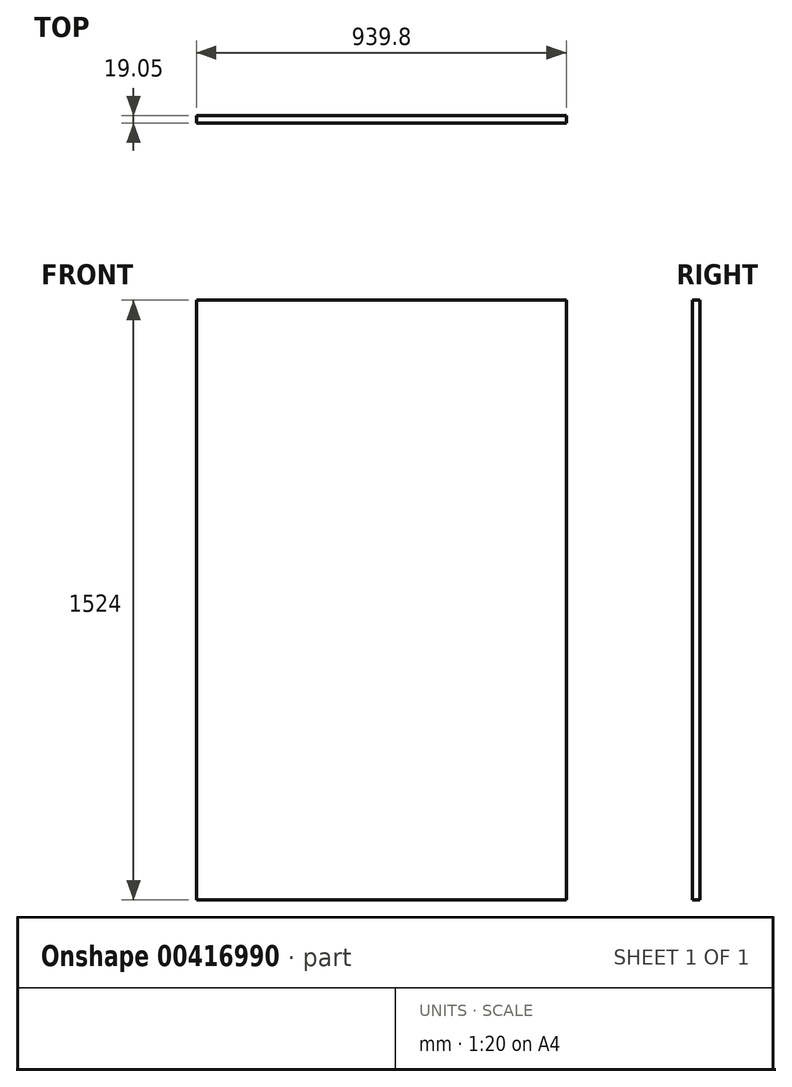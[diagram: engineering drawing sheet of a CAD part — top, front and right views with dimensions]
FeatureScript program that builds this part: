
annotation { "Feature Type Name" : "Feature", "Feature Type Description" : "" }
export const myFeature = defineFeature(function(context is Context, id is Id, definition is map)
    precondition{}
    {
        {
            var Q0;
            Q0=qCreatedBy(makeId("Front.planeOp"),FACE);
            var sketch = newSketch(context, id + "F0", { "sketchPlane" : qUnion([Q0])});
            skLineSegment(sketch, "E0.bottom", {"start": v(748.13, 187.42) * mm, "end": v(-191.67, 187.42) * mm});
            skLineSegment(sketch, "E0.top", {"start": v(748.13, -1336.58) * mm, "end": v(-191.67, -1336.58) * mm});
            skLineSegment(sketch, "E0.left", {"start": v(748.13, 187.42) * mm, "end": v(748.13, -1336.58) * mm});
            skLineSegment(sketch, "E0.right", {"start": v(-191.67, 187.42) * mm, "end": v(-191.67, -1336.58) * mm});
            skPoint(sketch, "E0.middle", {"position": v(278.23, -574.58) * mm});
            skSolve(sketch);
        }
        {
            var Q0;
            Q0=makeQuery(id+"F0.imprint","IMPRINT",FACE,{"disambiguationData":[TD([[makeQuery(id+"F0.imprint","IMPRINT",EDGE,{"derivedFrom":sQuery(id+"F0.wireOp",EDGE,"E0.bottom")}),1.0]])]});
            extrude(context, id + "F1", {"entities" : qUnion([Q0]), "depth" : 19.05 * mm});
        }
    });
